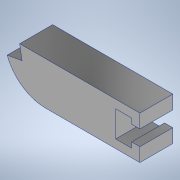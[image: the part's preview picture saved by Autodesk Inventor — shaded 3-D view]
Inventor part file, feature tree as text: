
AUTODESK INVENTOR PART (.ipt)
format: ipt  version: 2022 (Build 260153000, 153)  size: 157,696 bytes
history: native  units: mm
features: extrude x3, sketch x3, fillet x1
ambient origin geometry x8: Origin, YZ Plane, XZ Plane, XY Plane, X Axis, Y Axis, Z Axis, Center Point
bodies: Body1 (feature_tree)
feature tree (7):
  extrude  "Extrusion2"  Depth=5.8mm
  extrude  "Extrusion7"  Depth=12.0mm TaperAngle=0.0deg
  extrude  "Extrusion10"  Depth=15.6mm
  fillet  "Fillet2"  [1 undecoded]
  sketch  "Sketch5"  dims[d41=5.8mm d48=44.0mm]
  sketch  "Sketch11"  dims[d50=3.0mm d56=12.0mm d57=0.0mm]
  sketch  "Sketch14"  dims[d63=45.0mm d67=15.6mm d71=0.0mm d72=36.2mm d87=5.6mm d88=9.5mm d95=17.453293mm d96=5.0mm d97=10.0mm d98=0.0mm d99=0.0mm d107=5.5mm d108=0.0mm d109=0.0mm d110=15.0mm]
note: 1 required parameter value undecoded (feature->parameter linkage not recoverable at this tier; creation-order binding heuristic only, values carry confidence <= 0.55)
